# Revit family: Furniture-Wall_Mount-Vanity-KOHLER-Forefront-K-31601IN
name_source: partatom
category: Casework
units: mm (PartAtom-declared; Revit-internal decimal feet)

## family parameters
Cut with Voids When Loaded = No
Host = Face
OmniClass Number = 23.21.19.15.33
OmniClass Title = Residential Specialty Casework
Room Calculation Point = No
Shared = No

## types (3) — shared parameters
ADA Compliant = No
Assembly Code = E20
Construction Type = Wall Mount
Date Modified = 03/31/2023
Default Elevation = 35"
Description = Vanity 900 mm
Height = 22 11/16"
Length = 20 5/16"
Manufacturer = Kohler Co.
Master Format 2014 = 06 41 93
Master Format 2014 Name = Cabinet and Drawer Hardware
Material = Solid Wood Construction
Product Name = Forefront
URL = https://www.kohler.co.in
WaterSense Certified = No
Width = 35 1/8"

## per-type parameters (varying)
| type | Finish | Model | Product Documentation Link | Product Finish | Product Page URL | Type |
| C38-White Oak | Kohler-Wood-C38-White_Oak | K-31601IN-C38 |  | Kohler-Wood-C38-White_Oak |  | 1 |
| E63-Walnut | Kohler-Wood-E63-Walnut | K-31601IN-E63 | https://resources.kohler.com | Kohler-Wood-E63-Walnut | https://www.kohler.co.in | 2 |
| E64 | KOHLER-Wood-E64 | K-31601IN-E64 |  | KOHLER-Wood-E64 |  | 3 |

## geometry (parser evidence)
native form markers: Sweep x5
no freeform markers — native parametric forms only
